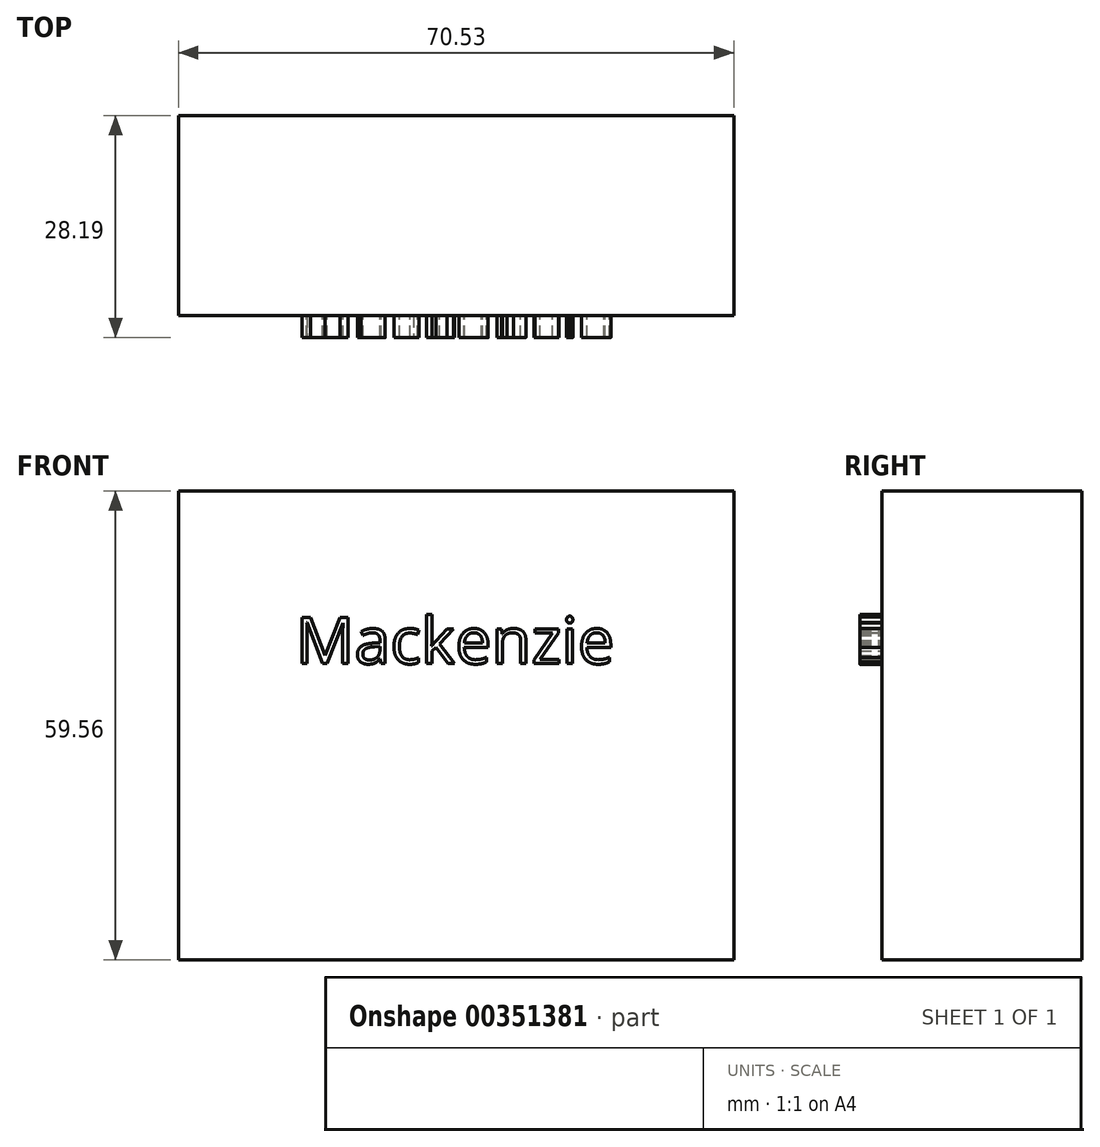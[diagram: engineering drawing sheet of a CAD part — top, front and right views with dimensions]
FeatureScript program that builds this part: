
annotation { "Feature Type Name" : "Feature", "Feature Type Description" : "" }
export const myFeature = defineFeature(function(context is Context, id is Id, definition is map)
    precondition{}
    {
        {
            var Q0;
            Q0=qCreatedBy(makeId("Front.planeOp"),FACE);
            var sketch = newSketch(context, id + "F0", { "sketchPlane" : qUnion([Q0])});
            skLineSegment(sketch, "E0.bottom", {"start": v(-33.04, 27.26) * mm, "end": v(37.49, 27.26) * mm});
            skLineSegment(sketch, "E0.top", {"start": v(-33.04, -32.3) * mm, "end": v(37.49, -32.3) * mm});
            skLineSegment(sketch, "E0.left", {"start": v(-33.04, 27.26) * mm, "end": v(-33.04, -32.3) * mm});
            skLineSegment(sketch, "E0.right", {"start": v(37.49, 27.26) * mm, "end": v(37.49, -32.3) * mm});
            skSolve(sketch);
        }
        {
            var Q0;
            Q0=makeQuery(id+"F0.imprint","IMPRINT",FACE,{"disambiguationData":[TD([[makeQuery(id+"F0.imprint","IMPRINT",EDGE,{"derivedFrom":sQuery(id+"F0.wireOp",EDGE,"E0.bottom")}),-1.0]])]});
            extrude(context, id + "F1", {"entities" : qUnion([Q0]), "depth" : 25.4 * mm});
        }
        {
            var Q0;
            Q0=qCreatedBy(makeId("Front.planeOp"),FACE);
            var sketch = newSketch(context, id + "F2", { "sketchPlane" : qUnion([Q0])});
            skText(sketch, "E1", { "text": "Mackenzie", "fontName": "OpenSans-Regular.ttf"});
            const initialGuessF2  = {"E1": [-0.01813, 0.00533, 1, 0, 0.00592]};
            skSetInitialGuess(sketch, initialGuessF2);
            skSolve(sketch);
        }
        {
            var Q0;
            Q0 = qSketchRegion(id + "F2", true);
            extrude(context, id + "F3", {"entities" : qUnion([Q0]), "operationType" : NewBodyOperationType.ADD, "depth" : 28.2 * mm});
        }
    });
